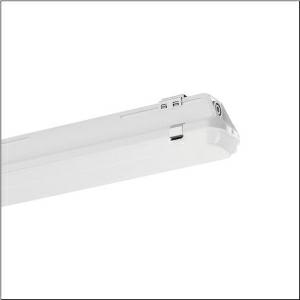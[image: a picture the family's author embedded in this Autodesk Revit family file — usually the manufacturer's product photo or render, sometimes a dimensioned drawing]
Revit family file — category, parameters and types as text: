
# Revit family: monsun_r__21_emergency_51fb207p437b3g_b246
name_source: partatom
category: Lighting Fixtures
units: mm (PartAtom-declared; Revit-internal decimal feet)

## family parameters
Cut with Voids When Loaded = No
Host = Face
Light Source = No
Part Type = Normal
Room Calculation Point = No
Round Connector Dimension = Use Diameter
Shared = No

## types (1)
- Monsun® 21 emergency (1 x LED, 3620 lm, 28 W, 4000K)
    Apparent Load = 28 VA
    CIE Flux Codes = 45 75 93 94 100
    Color Rendering = 80
    Color Temperature = 4000K
    Default Elevation = 1800 mm
    Description = Monsun® 21 emergency, damp-proof luminaire, chain hanger, primary optical cover: enclosure, of PC, light emission: direct distribution, primary light characteristic: symmetric, installation type: vertical mounting, horizontal mounting, surface-mounted, suspended mounting, LED, rated luminous flux: 3.620lm, luminous efficacy: 129lm/W, light colour: 840, colour temperature: 4000K, control gear: ECG, with terminal, 4-pole, max. 2.5mm², mains connection: 220..240V, AC, 50/60Hz, rated input power: 28W, control gear: single battery element, battery: NiCd, 4,5Ah, mains connection: 230V, housing, of glass-fibre reinforced polyester, uncoated, bright grey, length: 1.590mm, width: 90mm, height: 88mm, clip for enclosure, of stainless steel (V2A), ceiling mounting element, of stainless steel (V2A), chain hanger, of stainless steel (V2A), protection rating (complete): IP66, insulation class (complete): insulation class I (protective earthing), certification: CE, UKCA, protection symbol: D, impact resistance: IK08, permissible operating ambient temperature: +5..+25°C, standard: EN 60598-2-1, EN 50419, EN 60598-2-22, corresponds to IFS (International Featured Standards) requirements for safety and quality in the food industry, for indoor or canopied outdoor use, no direct snow, no direct sun, no direct rain, packaging unit: 1 piece
    Height = 89 mm
    Lamp = 1 x LED
    Lamp Light Flux = 3620 lm
    Lamp Power = 28 W
    Lamp count = 1
    Length = 1590 mm
    Luminous efficacy = 129 lm/W
    Manufacturer = Siteco
    ModVariant = No
    Model = 51FB207P437B3G
    Mounting Place = Ceiling
    Mounting Type = Pendant
    Number of Poles = 1
    OnlyDefault = Yes
    Power Factor = 1
    Product Name = Monsun® 21 emergency
    Product group = damp-proof luminaire | ceiling pendant
    ProductGroupID = 908
    Protection Class = Protection class I
    Protection Degree = IP 66
    RLX_Detail_Level = 1
    RlxData = <blob elided: 88665 chars, md5=baa6d1c2>
    Socket = socket
    Standby Power = 0 W
    System Light Flux = 3620 lm
    System Power = 28 W
    Type Comments = Product without accessories
    Type Image = l_1006717.jpg
    URL = http://relux.com
    VarID = ---
    Voltage = 0 V
    Weight = 0.00 kg
    Width = 90 mm

## geometry (parser evidence)
native form markers: Blend x4, Sweep x13
no freeform markers — native parametric forms only
